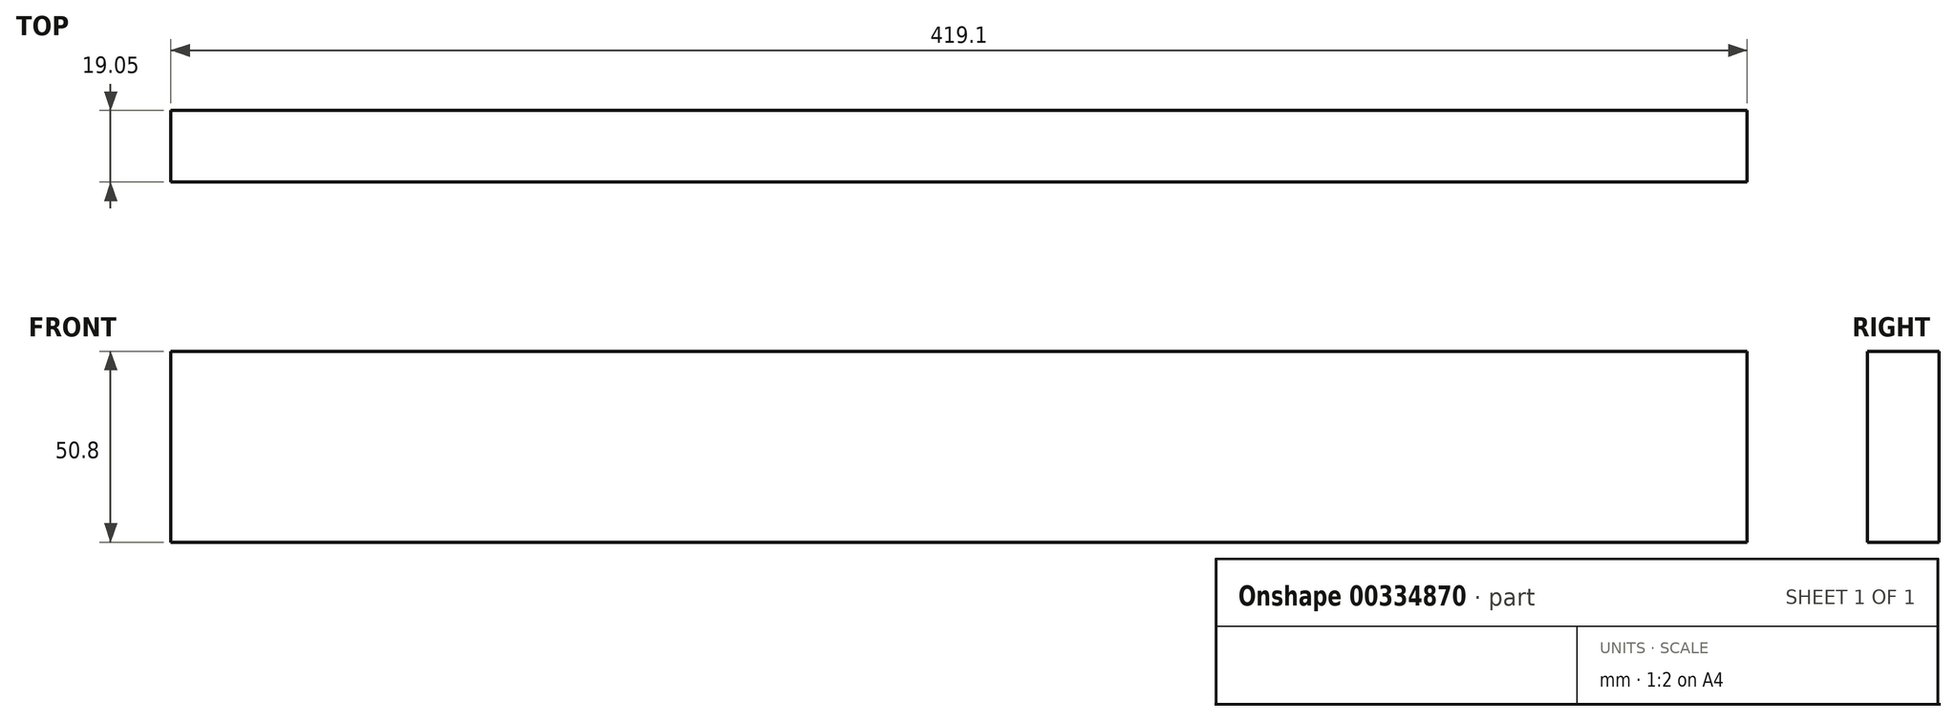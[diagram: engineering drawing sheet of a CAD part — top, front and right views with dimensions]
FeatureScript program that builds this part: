
annotation { "Feature Type Name" : "Feature", "Feature Type Description" : "" }
export const myFeature = defineFeature(function(context is Context, id is Id, definition is map)
    precondition{}
    {
        {
            var Q0;
            Q0=qCreatedBy(makeId("Top.planeOp"),FACE);
            var sketch = newSketch(context, id + "F0", { "sketchPlane" : qUnion([Q0])});
            skLineSegment(sketch, "E0.bottom", {"start": v(-209.55, 9.7) * mm, "end": v(209.55, 9.7) * mm});
            skLineSegment(sketch, "E0.top", {"start": v(-209.55, -9.35) * mm, "end": v(209.55, -9.35) * mm});
            skLineSegment(sketch, "E0.left", {"start": v(-209.55, 9.7) * mm, "end": v(-209.55, -9.35) * mm});
            skLineSegment(sketch, "E0.right", {"start": v(209.55, 9.7) * mm, "end": v(209.55, -9.35) * mm});
            skSolve(sketch);
        }
        {
            var Q0;
            Q0=makeQuery(id+"F0.imprint","IMPRINT",FACE,{"disambiguationData":[TD([[makeQuery(id+"F0.imprint","IMPRINT",EDGE,{"derivedFrom":sQuery(id+"F0.wireOp",EDGE,"E0.bottom")}),-1.0]])]});
            extrude(context, id + "F1", {"entities" : qUnion([Q0]), "depth" : 50.8 * mm});
        }
    });
